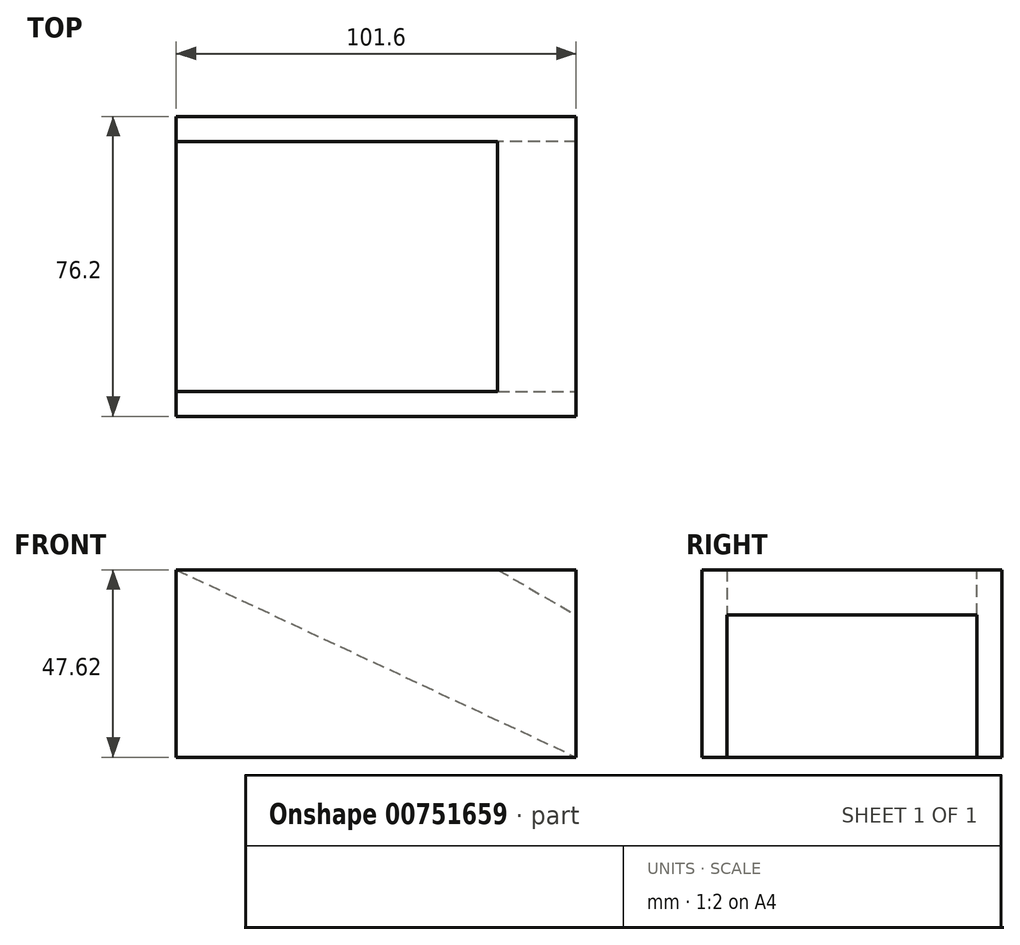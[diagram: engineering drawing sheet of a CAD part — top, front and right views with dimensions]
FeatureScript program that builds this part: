
annotation { "Feature Type Name" : "Feature", "Feature Type Description" : "" }
export const myFeature = defineFeature(function(context is Context, id is Id, definition is map)
    precondition{}
    {
        {
            var Q0;
            Q0=qCreatedBy(makeId("Front.planeOp"),FACE);
            var sketch = newSketch(context, id + "F0", { "sketchPlane" : qUnion([Q0])});
            skLineSegment(sketch, "E0.bottom", {"start": v(50.8, 23.81) * mm, "end": v(-50.8, 23.81) * mm});
            skLineSegment(sketch, "E0.top", {"start": v(50.8, -23.81) * mm, "end": v(-50.8, -23.81) * mm});
            skLineSegment(sketch, "E0.left", {"start": v(50.8, 23.81) * mm, "end": v(50.8, -23.81) * mm});
            skLineSegment(sketch, "E0.right", {"start": v(-50.8, 23.81) * mm, "end": v(-50.8, -23.81) * mm});
            skPoint(sketch, "E0.middle", {"position": v(0, 0) * mm});
            skLineSegment(sketch, "E1", {"start": v(30.84, 23.81) * mm, "end": v(50.8, 12.29) * mm});
            skLineSegment(sketch, "E2", {"start": v(-50.8, 23.81) * mm, "end": v(50.8, -23.81) * mm});
            skSolve(sketch);
        }
        {
            var Q0;
            {var subQ3=sQuery(id+"F0.wireOp",EDGE,"E1");Q0=makeQuery(id+"F0.imprint","IMPRINT",FACE,{"disambiguationData":[TD([[makeQuery(id+"F0.imprint","IMPRINT",EDGE,{"derivedFrom":subQ3}),1.0]])]});}
            var Q1;
            {var subQ1=sQuery(id+"F0.wireOp",EDGE,"E0.top");var subQ3=sQuery(id+"F0.wireOp",EDGE,"fsyc6oh1-RzGM-H65r-f2Ob-yatIOPQvbFgo");var subQ4=makeQuery(id+"F0.imprint","INTERSECT",VERTEX,{"derivedFrom":[subQ1,subQ3]});Q1=makeQuery(id+"F0.imprint","IMPRINT",FACE,{"disambiguationData":[TD([[makeQuery(id+"F0.imprint","IMPRINT",EDGE,{"disambiguationData":[TD([[subQ4,1.0]])],"derivedFrom":subQ3}),1.0]])]});}
            var Q2;
            {var subQ0=sQuery(id+"F0.wireOp",EDGE,"E0.right");Q2=makeQuery(id+"F0.imprint","IMPRINT",FACE,{"disambiguationData":[TD([[makeQuery(id+"F0.imprint","IMPRINT",EDGE,{"derivedFrom":subQ0}),1.0]])]});}
            var Q3;
            {var subQ6=sQuery(id+"F0.wireOp",EDGE,"E0.left");Q3=makeQuery(id+"F0.imprint","IMPRINT",FACE,{"disambiguationData":[TD([[makeQuery(id+"F0.imprint","IMPRINT",EDGE,{"derivedFrom":subQ6}),-1.0]])]});}
            extrude(context, id + "F1", {"entities" : qUnion([Q0, Q1, Q2, Q3]), "endBound" : BoundingType.SYMMETRIC, "depth" : 76.2 * mm, "offsetDistance" : 25.4 * mm});
        }
        {
            var Q0;
            Q0=makeQuery(id+"F1.opExtrude","CAP_FACE",FACE,{"disambiguationData":[OSD([sQuery(id+"F0.wireOp",EDGE,"E0.bottom"),sQuery(id+"F0.wireOp",EDGE,"E0.left"),sQuery(id+"F0.wireOp",EDGE,"E1")])],"isStart":true});
            var sketch = newSketch(context, id + "F2", { "sketchPlane" : qUnion([Q0])});
            skLineSegment(sketch, "E3.bottom", {"start": v(-50.8, 23.81) * mm, "end": v(50.8, 23.81) * mm});
            skLineSegment(sketch, "E3.top", {"start": v(-50.8, -23.81) * mm, "end": v(50.8, -23.81) * mm});
            skLineSegment(sketch, "E3.left", {"start": v(-50.8, 23.81) * mm, "end": v(-50.8, -23.81) * mm});
            skLineSegment(sketch, "E3.right", {"start": v(50.8, 23.81) * mm, "end": v(50.8, -23.81) * mm});
            skPoint(sketch, "E3.middle", {"position": v(0, 0) * mm});
            skSolve(sketch);
        }
        {
            var Q0;
            Q0 = qSketchRegion(id + "F2", true);
            extrude(context, id + "F3", {"entities" : qUnion([Q0]), "operationType" : NewBodyOperationType.ADD, "oppositeDirection" : true, "depth" : 6.35 * mm, "offsetDistance" : 25.4 * mm});
        }
        {
            var Q0;
            Q0=makeQuery(id+"F1.opExtrude","CAP_FACE",FACE,{"disambiguationData":[OSD([sQuery(id+"F0.wireOp",EDGE,"E0.top"),sQuery(id+"F0.wireOp",EDGE,"E0.right"),sQuery(id+"F0.wireOp",EDGE,"E2")])],"isStart":false});
            var sketch = newSketch(context, id + "F4", { "sketchPlane" : qUnion([Q0])});
            skLineSegment(sketch, "E4.bottom", {"start": v(50.8, -23.81) * mm, "end": v(-50.8, -23.81) * mm});
            skLineSegment(sketch, "E4.top", {"start": v(50.8, 23.81) * mm, "end": v(-50.8, 23.81) * mm});
            skLineSegment(sketch, "E4.left", {"start": v(50.8, -23.81) * mm, "end": v(50.8, 23.81) * mm});
            skLineSegment(sketch, "E4.right", {"start": v(-50.8, -23.81) * mm, "end": v(-50.8, 23.81) * mm});
            skPoint(sketch, "E4.middle", {"position": v(0, 0) * mm});
            skSolve(sketch);
        }
        {
            var Q0;
            Q0 = qSketchRegion(id + "F4", true);
            extrude(context, id + "F5", {"entities" : qUnion([Q0]), "operationType" : NewBodyOperationType.ADD, "oppositeDirection" : true, "depth" : 6.35 * mm, "offsetDistance" : 25.4 * mm});
        }
    });
